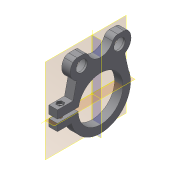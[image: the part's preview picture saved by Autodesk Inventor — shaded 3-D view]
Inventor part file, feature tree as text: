
AUTODESK INVENTOR PART (.ipt)
format: ipt  version: 2015 SP2 (Build 190223200, 223)  size: 198,144 bytes
history: native  units: mm
features: sketch x6, extrude x5, other x1, hole x1
ambient origin geometry x8: Origin, YZ Plane, XZ Plane, XY Plane, X Axis, Y Axis, Z Axis, Center Point
bodies: Body1 (feature_tree)
feature tree (13):
  other  "Sólido1"
  extrude  "Extrusión1"  Depth=63.5mm
  extrude  "Extrusión2"  Depth=15.5mm
  extrude  "Extrusión3"  Depth=4.5mm
  hole  "Agujero1"  [1 undecoded]
  extrude  "Extrusión4"  Depth=7.5mm
  extrude  "Extrusión5"  Depth=9.0mm TaperAngle=0.0deg
  sketch  "Boceto1"  dims[d0=47.5mm d1=63.5mm]
  sketch  "Boceto2"  dims[d2=4.464552mm d4=15.5mm]
  sketch  "Boceto3"  dims[d5=15.5mm d7=4.5mm]
  sketch  "Boceto4"  dims[d8=4.5mm d15=9.0mm d16=0.0mm]
  sketch  "Boceto5"  dims[d17=8.5mm d18=7.5mm]
  sketch  "Boceto6"  dims[d19=4.0mm d22=9.0mm d23=0.0mm d25=51.027mm d26=22.0mm d27=37.4mm d31=12.0mm d32=12.0mm d34=2.0mm d35=0.0mm d37=3.75mm d38=6.0mm d39=4.0mm d40=2.0mm d41=90.0deg d42=8.0mm d43=20.594885mm d44=6.235mm d45=2.8mm d46=0.0mm d50=10.0mm d51=10.0mm d52=0.0mm d55=10.0mm d58=40.0mm d59=20.0mm d60=40.0mm d61=52.0mm d62=14.0mm d63=6.0mm d64=6.0mm]
note: 1 required parameter value undecoded (feature->parameter linkage not recoverable at this tier; creation-order binding heuristic only, values carry confidence <= 0.55)
